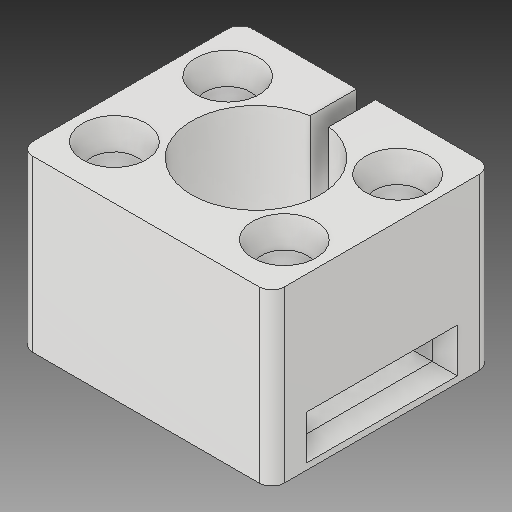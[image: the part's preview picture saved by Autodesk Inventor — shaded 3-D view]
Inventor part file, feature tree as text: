
AUTODESK INVENTOR PART (.ipt)
format: ipt  version: 2019 (Build 230136000, 136)  size: 243,712 bytes
history: native  units: mm
features: sketch x9, extrude x7, loft x4, plane x1, fillet x1, chamfer x1
ambient origin geometry x8: Origin, YZ Plane, XZ Plane, XY Plane, X Axis, Y Axis, Z Axis, Center Point
bodies: Solid1 (feature_tree)
feature tree (23):
  extrude  "Extrusion1"  Depth=40.0mm
  extrude  "Extrusion2"  Depth=21.0mm
  extrude  "Extrusion3"  Depth=3.0mm
  extrude  "Extrusion4"  Depth=11.0mm TaperAngle=0.0deg
  sketch  "Sketch6"  dims[d11=14.5mm d12=3.0mm d13=0.0mm]
  plane  "Work Plane1"
  sketch  "Sketch7"  dims[d14=18.0mm d15=27.0mm]
  loft  "Loft2"
  loft  "Loft3"
  loft  "Loft4"
  loft  "Loft5"
  extrude  "Extrusion6"  TaperAngle=0.0deg  [1 undecoded]
  extrude  "Extrusion7"  TaperAngle=0.0deg  [1 undecoded]
  fillet  "Fillet1"  [1 undecoded]
  chamfer  "Chamfer1"  Angle=90.0deg  [1 undecoded]
  extrude  "Extrusion8"  TaperAngle=0.0deg  [1 undecoded]
  sketch  "Sketch1"  dims[d0=35.0mm d1=40.0mm]
  sketch  "Sketch2"  dims[d2=21.0mm d3=0.0mm d4=20.4mm]
  sketch  "Sketch3"  dims[d5=15.0mm d6=0.0mm d7=3.0mm]
  sketch  "Sketch5"  dims[d8=4.5mm d9=11.0mm d10=0.0mm]
  sketch  "Sketch8"  dims[d16=10.1mm d19=17.0mm]
  sketch  "Sketch9"  dims[d20=7.3mm d21=27.0mm]
  sketch  "Sketch10"  dims[d22=18.0mm d27=0.0mm d28=90.0deg d29=0.0mm d30=90.0deg d31=0.0mm d32=90.0deg d33=0.0mm d34=90.0deg d35=0.0mm d36=90.0deg d37=0.0mm d38=90.0deg d39=0.0mm d40=90.0deg d41=0.0mm d42=90.0deg d43=10.4mm d46=3.0mm d47=0.0mm d48=3.0mm d49=0.0mm d50=20.0mm d51=2.0mm d52=2.0mm d53=2.0mm d54=45.0deg d55=20.0mm d56=25.0mm d57=4.0mm d58=10.0mm d59=0.0mm]
note: 5 required parameter values undecoded (feature->parameter linkage not recoverable at this tier; creation-order binding heuristic only, values carry confidence <= 0.55)
